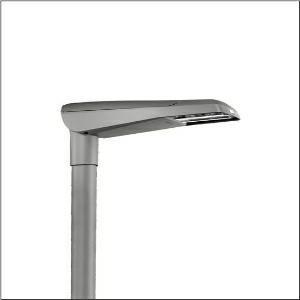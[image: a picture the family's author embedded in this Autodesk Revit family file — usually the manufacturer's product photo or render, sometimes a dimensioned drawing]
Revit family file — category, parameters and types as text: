
# Revit family: streetlight_sl_11_iq_micro___st0_5a_5xc1bc1f08de_0799
name_source: partatom
category: Lighting Fixtures
units: mm (PartAtom-declared; Revit-internal decimal feet)

## family parameters
Cut with Voids When Loaded = No
Host = Face
Light Source = No
Part Type = Normal
Room Calculation Point = No
Round Connector Dimension = Use Diameter
Shared = No

## types (1)
- --- (1 x LED, 3820 lm, 27.4 W, 4000K)
    Apparent Load = 27 VA
    CIE Flux Codes = 42 72 97 100 100
    Color Rendering = 70
    Color Temperature = 4000K
    Default Elevation = 1800 mm
    Description = Streetlight SL 11 iQ micro, mast luminaire, primary light control with 3 zone facetted reflector, of plastic, silver coated, highly specular, primary optical cover: cover, of PMMA, transparent, light distribution: ST0.5a, light emission: direct distribution, primary light characteristic: asymmetric, installation type: post-top, side-entry, lamps: LED, High Power LED, rated values: 3.590lm | 27,7W | 129,6lm/W (begin service life); end service life: 3.590lm | 28,1W; at 50% lumin. flux: 1.795lm | 13,4W | 134lm/W, colour temperature: 2200/2700/3000/4000K, colour rendering: CRI > 70, light colour: 722/727/730/740, light setting 1 begin service life: 100% | 3.590lm | 27,7W | 129,6lm/W | 3.000K, light setting 1 end service life: 28,1W, further light settings possible, control: Street-Remote, Auto-Match, Temp-Guard, Lumen-Switch, Night-Set, Smart-Wire, Light-Fading, Desk-Remote (wireless, voltage-free reading and setting of iQ features in the workshop via application-optimized NFC function/RFID function), optimised constant luminous flux control (CLO 2.0), with cable H07RN-F 5x 1.5mm², mains connection: 220..240V, AC, 50/60Hz, connection cable pre-assembled, cable length: 6,5m, luminaire housing, of diecast aluminium, powder-coated, Siteco® metallic grey (DB 702S), please order mast flange separately, inclination adjustable without tools: 0°, 5°, 10°, 15° (post-top) | 0°, -5°, -10°, -15° (side-entry), sealing non-destructively replaceable, multi-level sealing system, length: 600mm, width: 174mm, height: 116mm, mast flange for spigot size: 42mm (side-entry): 5XC10008XM4, 60/48mm (side-entry/post-top): 5XC10108XM2, 76/60mm (side-entry/post-top): 5XC10108XM1, equipment: Power, protection rating (complete): IP66, insulation class (complete): insulation class II (safety insulation), certification: CE, ENEC, ENEC+, VDE, impact resistance: IK10, permissible operating ambient temperature for outdoor applications: -25..+50°C, standard-compliant lighting for roads and squares, Environmental Product Declaration (EPD) tested and certified by an independent institute, packaging unit: 1 piece

Light Distribution: ST0.5a
    Height = 116 mm
    Lamp = 1 x LED
    Lamp Light Flux = 3820 lm
    Lamp Power = 27.4 W
    Lamp count = 1
    Length = 600 mm
    Luminous efficacy = 139 lm/W
    Manufacturer = Siteco
    ModVariant = No
    Model = 5XC1BC1F08DE
    Number of Poles = 1
    OnlyDefault = Yes
    Power Factor = 1
    Product Name = Streetlight SL 11 iQ micro | ST0.5a
    Product group = mast luminaire | pylon top
    ProductGroupID = 6100
    Protection Class = Protection class II
    Protection Degree = IP 66
    RLX_Detail_Level = 1
    RLX_Emergency_Light_Flux = 0 lm
    RLX_Emergency_Type = 0
    RLX_Emergency_Type_DB = No
    RlxData = <blob elided: 59393 chars, md5=7564c216>
    Socket = socket
    Standby Power = 0 W
    System Light Flux = 3820 lm
    System Power = 27 W
    Type Comments = individual setting: luminous flux: 100 % | dim-lin: 254 | 726 mA
    Type Image = l_1006566.jpg
    URL = http://relux.com
    VarID = @adj_062189
    Voltage = 0 V
    Weight = 0.00 kg
    Width = 174 mm

## geometry (parser evidence)
native form markers: Blend x4, Sweep x12
no freeform markers — native parametric forms only
